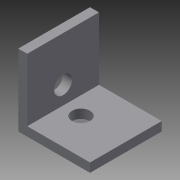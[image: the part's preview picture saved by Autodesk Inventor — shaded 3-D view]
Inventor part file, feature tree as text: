
AUTODESK INVENTOR PART (.ipt)
format: ipt  version: 2014 (Build 180170000, 170)  size: 92,672 bytes
history: native  units: in
note: dims shown in document units (in); Inventor stores cm internally (conversion verified against a paired STEP export)
features: sketch x3, hole x2, extrude x1
ambient origin geometry x8: Origin, YZ Plane, XZ Plane, XY Plane, X Axis, Y Axis, Z Axis, Center Point
bodies: Solid1 (feature_tree)
feature tree (6):
  extrude  "Extrusion1"  Depth=0.125in
  hole  "Hole1"  [1 undecoded]
  hole  "Hole2"  [1 undecoded]
  sketch  "Sketch1"  dims[d0=1.0in d1=0.125in]
  sketch  "Sketch2"  dims[d2=0.875in d3=0.875in]
  sketch  "Sketch3"  dims[d4=0.125in d5=1.0in d6=0.0in d7=0.375in d8=0.25in d9=0.75in d10=0.375in d11=0.25in d12=0.5635in d13=1.0in d14=0.8108in d15=0.375in d16=0.25in d17=0.75in d18=0.375in d19=0.25in d20=0.5635in d21=1.0in d22=0.8108in]
note: 2 required parameter values undecoded (feature->parameter linkage not recoverable at this tier; creation-order binding heuristic only, values carry confidence <= 0.55)
